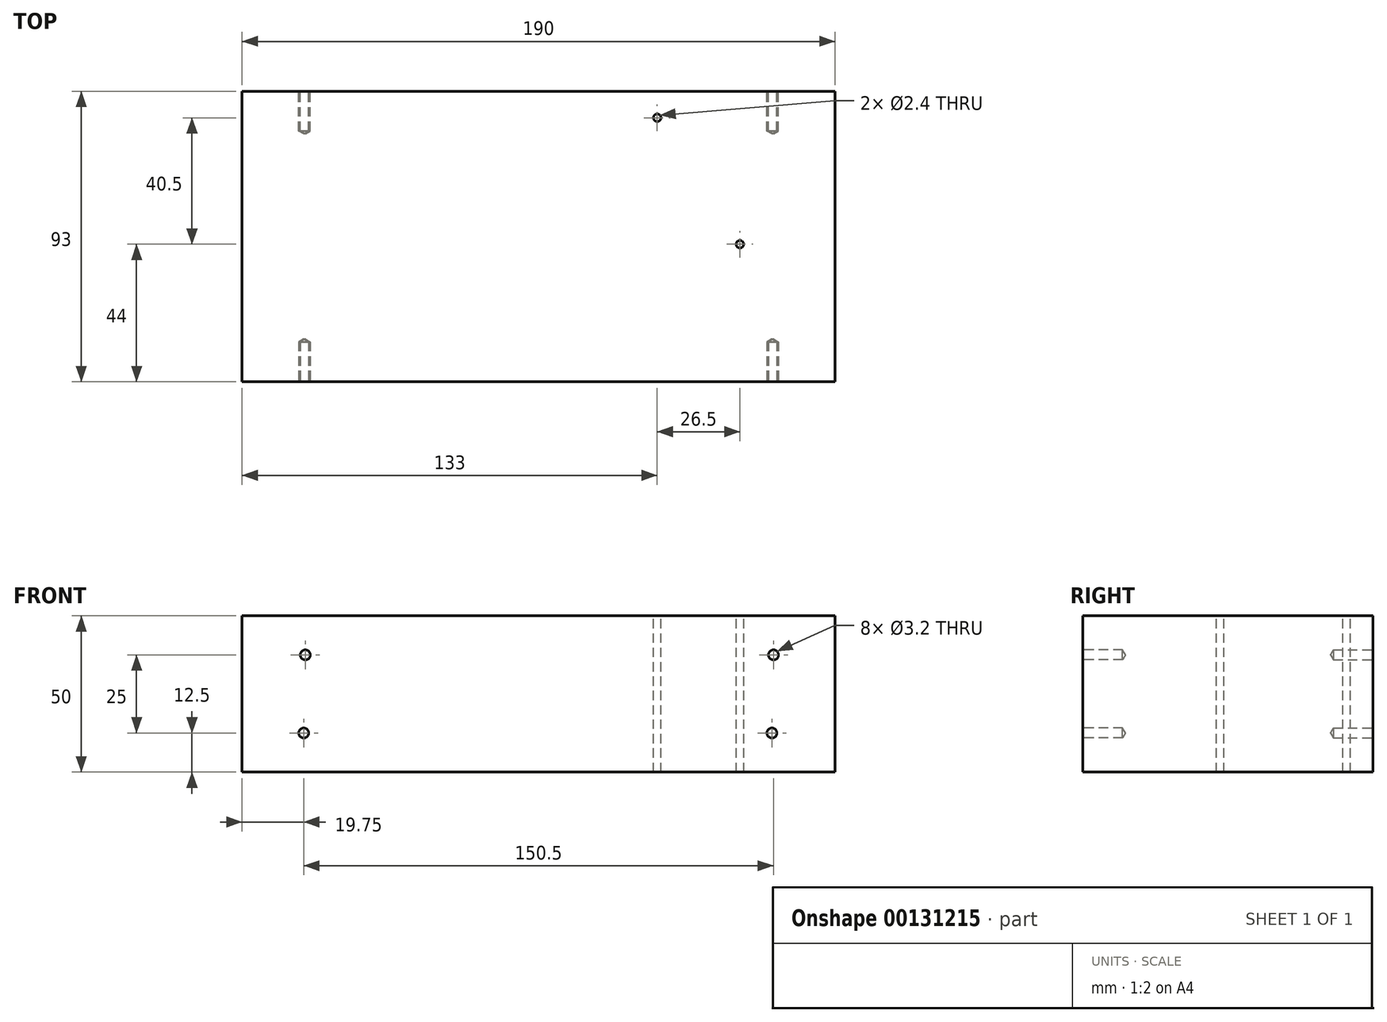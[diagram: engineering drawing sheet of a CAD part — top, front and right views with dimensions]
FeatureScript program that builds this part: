
annotation { "Feature Type Name" : "Feature", "Feature Type Description" : "" }
export const myFeature = defineFeature(function(context is Context, id is Id, definition is map)
    precondition{}
    {
        {
            var Q0;
            Q0=qCreatedBy(makeId("Front.planeOp"),FACE);
            var sketch = newSketch(context, id + "F0", { "sketchPlane" : qUnion([Q0])});
            skLineSegment(sketch, "E0.bottom", {"start": v(-95, 25) * mm, "end": v(95, 25) * mm});
            skLineSegment(sketch, "E0.top", {"start": v(-95, -25) * mm, "end": v(95, -25) * mm});
            skLineSegment(sketch, "E0.left", {"start": v(-95, 25) * mm, "end": v(-95, -25) * mm});
            skLineSegment(sketch, "E0.right", {"start": v(95, 25) * mm, "end": v(95, -25) * mm});
            skPoint(sketch, "E0.middle", {"position": v(0, 0) * mm});
            skSolve(sketch);
        }
        {
            var Q0;
            Q0=makeQuery(id+"F0.imprint","IMPRINT",FACE,{"disambiguationData":[TD([[makeQuery(id+"F0.imprint","IMPRINT",EDGE,{"derivedFrom":sQuery(id+"F0.wireOp",EDGE,"E0.bottom")}),-1.0]])]});
            extrude(context, id + "F1", {"entities" : qUnion([Q0]), "depth" : 93 * mm});
        }
        {
            var Q0;
            Q0=makeQuery(id+"F1.opExtrude","CAP_FACE",FACE,{"disambiguationData":[OSD([sQuery(id+"F0.wireOp",EDGE,"E0.bottom"),sQuery(id+"F0.wireOp",EDGE,"E0.top"),sQuery(id+"F0.wireOp",EDGE,"E0.left"),sQuery(id+"F0.wireOp",EDGE,"E0.right")])],"isStart":false});
            var sketch = newSketch(context, id + "F2", { "sketchPlane" : qUnion([Q0])});
            skPoint(sketch, "E1", {"position": v(-74.75, 12.5) * mm});
            skPoint(sketch, "E2", {"position": v(75.25, 12.5) * mm});
            skPoint(sketch, "E3", {"position": v(74.75, -12.5) * mm});
            skPoint(sketch, "E4", {"position": v(-75.25, -12.5) * mm});
            skSolve(sketch);
        }
        {
            var Q0;
            Q0=sQuery(id+"F2.wireOp",VERTEX,"E1");
            var Q1;
            Q1=sQuery(id+"F2.wireOp",VERTEX,"E2");
            var Q2;
            Q2=sQuery(id+"F2.wireOp",VERTEX,"E3");
            var Q3;
            Q3=sQuery(id+"F2.wireOp",VERTEX,"E4");
            var Q4;
            Q4=makeQuery(id+"F1.opExtrude","SWEPT_BODY",BODY,{"disambiguationData":[OSD([sQuery(id+"F0.wireOp",EDGE,"E0.bottom"),sQuery(id+"F0.wireOp",EDGE,"E0.top"),sQuery(id+"F0.wireOp",EDGE,"E0.left"),sQuery(id+"F0.wireOp",EDGE,"E0.right")])]});
            hole(context, id + "F3", {"style" : HoleStyle.SIMPLE, "endStyle" : HoleEndStyle.BLIND, "standardTappedOrClearance" : lookupTablePath({ "standard" : "ISO", "engagement" : "75%", "pitch" : "0.75 mm", "size" : "M4", "type" : "Tapped" }), "standardBlindInLast" : lookupTablePath({ "standard" : "ISO", "engagement" : "75%", "pitch" : "0.75 mm", "size" : "M4", "type" : "Tapped" }), "holeDiameter" : 3.2 * mm, "holeDepth" : 12.7 * mm, "locations" : qUnion([Q0, Q1, Q2, Q3]), "scope" : qUnion([Q4])});
        }
        {
            var Q0;
            Q0=makeQuery(id+"F1.opExtrude","CAP_FACE",FACE,{"disambiguationData":[OSD([sQuery(id+"F0.wireOp",EDGE,"E0.bottom"),sQuery(id+"F0.wireOp",EDGE,"E0.top"),sQuery(id+"F0.wireOp",EDGE,"E0.left"),sQuery(id+"F0.wireOp",EDGE,"E0.right")])],"isStart":true});
            var sketch = newSketch(context, id + "F4", { "sketchPlane" : qUnion([Q0])});
            skCircle(sketch, "E5.0", {"center": v(74.75, 12.5) * mm, "radius": 1.6 * mm, "construction": true});
            skCircle(sketch, "E6.0", {"center": v(75.25, -12.5) * mm, "radius": 1.6 * mm, "construction": true});
            skCircle(sketch, "E7.0", {"center": v(-74.75, -12.5) * mm, "radius": 1.6 * mm, "construction": true});
            skCircle(sketch, "E8.0", {"center": v(-75.25, 12.5) * mm, "radius": 1.6 * mm, "construction": true});
            skSolve(sketch);
        }
        {
            var Q0;
            Q0=sQuery(id+"F4.wireOp",VERTEX,"E8.0.center");
            var Q1;
            Q1=sQuery(id+"F4.wireOp",VERTEX,"E5.0.center");
            var Q2;
            Q2=sQuery(id+"F4.wireOp",VERTEX,"E6.0.center");
            var Q3;
            Q3=sQuery(id+"F4.wireOp",VERTEX,"E7.0.center");
            var Q4;
            Q4=makeQuery(id+"F1.opExtrude","SWEPT_BODY",BODY,{"disambiguationData":[OSD([sQuery(id+"F0.wireOp",EDGE,"E0.bottom"),sQuery(id+"F0.wireOp",EDGE,"E0.top"),sQuery(id+"F0.wireOp",EDGE,"E0.left"),sQuery(id+"F0.wireOp",EDGE,"E0.right")])]});
            hole(context, id + "F5", {"style" : HoleStyle.SIMPLE, "endStyle" : HoleEndStyle.BLIND, "standardTappedOrClearance" : lookupTablePath({ "standard" : "ISO", "engagement" : "75%", "pitch" : "0.75 mm", "size" : "M4", "type" : "Tapped" }), "standardBlindInLast" : lookupTablePath({ "standard" : "ISO", "engagement" : "75%", "pitch" : "0.75 mm", "size" : "M4", "type" : "Tapped" }), "holeDiameter" : 3.2 * mm, "holeDepth" : 12.7 * mm, "locations" : qUnion([Q0, Q1, Q2, Q3]), "scope" : qUnion([Q4])});
        }
        {
            var Q0;
            Q0=makeQuery(id+"F1.opExtrude","SWEPT_FACE",FACE,{"disambiguationData":[OSD([sQuery(id+"F0.wireOp",EDGE,"E0.bottom")])]});
            var sketch = newSketch(context, id + "F6", { "sketchPlane" : qUnion([Q0])});
            skPoint(sketch, "E9", {"position": v(38, -8.5) * mm});
            skPoint(sketch, "E10", {"position": v(64.5, -49) * mm});
            skSolve(sketch);
        }
        {
            var Q0;
            Q0=sQuery(id+"F6.wireOp",VERTEX,"E9");
            var Q1;
            Q1=sQuery(id+"F6.wireOp",VERTEX,"E10");
            var Q2;
            Q2=makeQuery(id+"F1.opExtrude","SWEPT_BODY",BODY,{"disambiguationData":[OSD([sQuery(id+"F0.wireOp",EDGE,"E0.bottom"),sQuery(id+"F0.wireOp",EDGE,"E0.top"),sQuery(id+"F0.wireOp",EDGE,"E0.left"),sQuery(id+"F0.wireOp",EDGE,"E0.right")])]});
            hole(context, id + "F7", {"style" : HoleStyle.SIMPLE, "endStyle" : HoleEndStyle.THROUGH, "standardTappedOrClearance" : lookupTablePath({ "standard" : "ISO", "engagement" : "75%", "pitch" : "0.6 mm", "size" : "M3", "type" : "Tapped" }), "standardBlindInLast" : lookupTablePath({ "standard" : "ISO", "engagement" : "75%", "pitch" : "0.6 mm", "size" : "M3", "type" : "Tapped" }), "holeDiameter" : 2.4 * mm, "locations" : qUnion([Q0, Q1]), "scope" : qUnion([Q2]), "isTappedThrough" : true, "showTappedDepth" : true});
        }
    });
